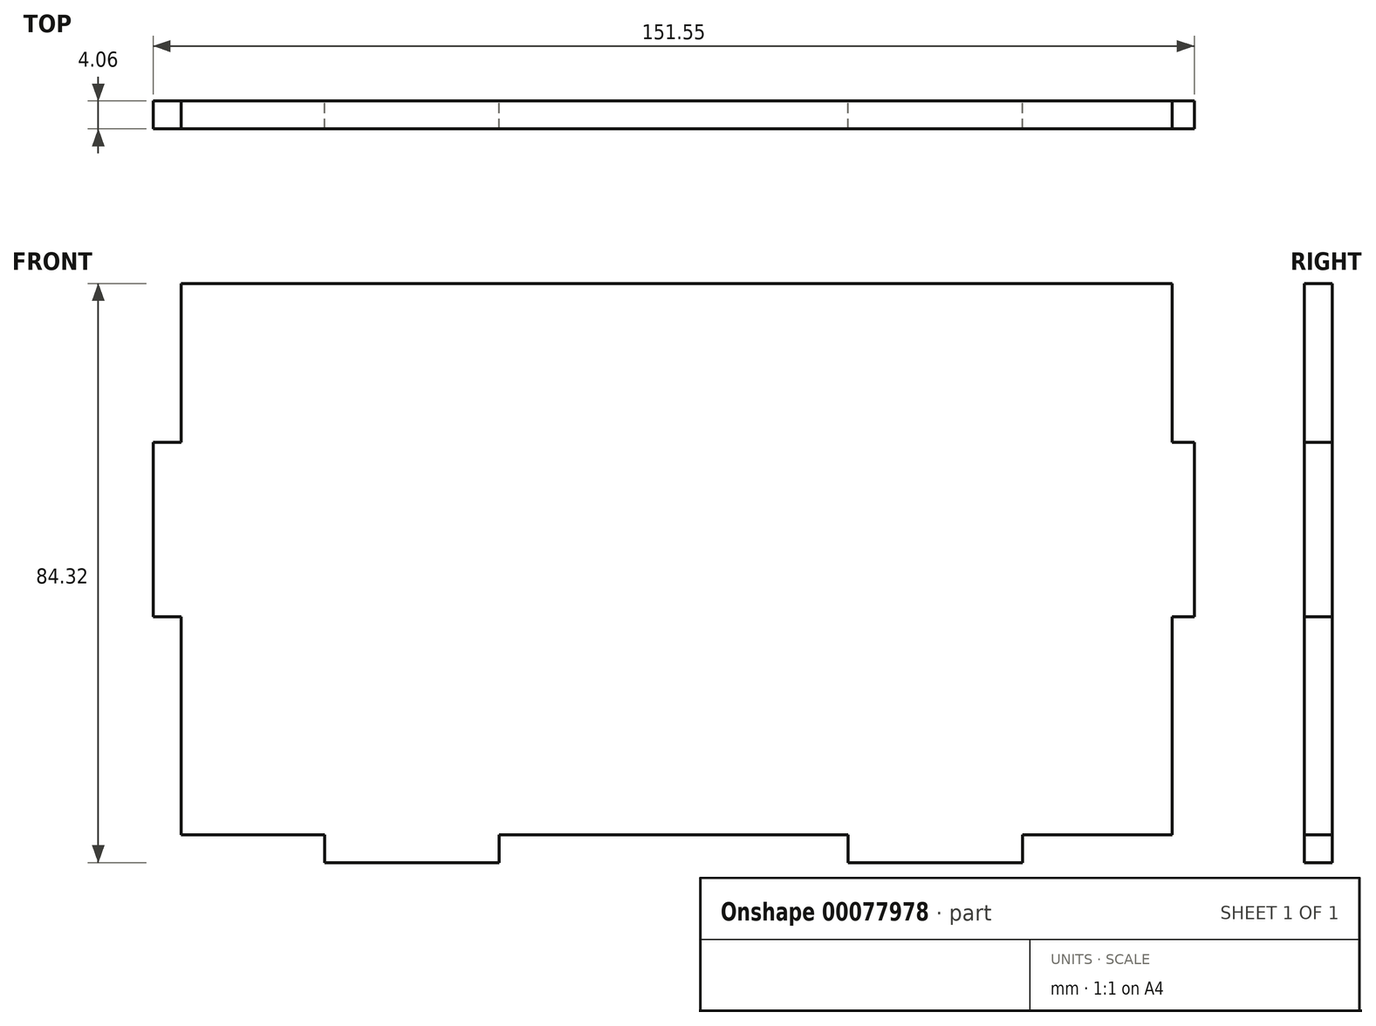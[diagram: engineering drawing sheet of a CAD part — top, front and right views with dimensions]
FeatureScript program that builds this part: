
annotation { "Feature Type Name" : "Feature", "Feature Type Description" : "" }
export const myFeature = defineFeature(function(context is Context, id is Id, definition is map)
    precondition{}
    {
        {
            var Q0;
            Q0=qCreatedBy(makeId("Front.planeOp"),FACE);
            var sketch = newSketch(context, id + "F0", { "sketchPlane" : qUnion([Q0])});
            skLineSegment(sketch, "E0.top", {"start": v(-104.23, 10.4) * mm, "end": v(-83.32, 10.4) * mm});
            skLineSegment(sketch, "E0.right", {"start": v(40.04, 86.6) * mm, "end": v(40.04, 67.55) * mm});
            skLineSegment(sketch, "E1.trimOffspring", {"start": v(-13.04, 10.4) * mm, "end": v(-7.12, 10.4) * mm});
            skPoint(sketch, "E2.orphan", {"position": v(-32.1, 10.4) * mm});
            skPoint(sketch, "E3.endSnap0", {"position": v(-32.1, 60.31) * mm});
            skLineSegment(sketch, "E4.top", {"start": v(-83.32, 90.66) * mm, "end": v(-57.92, 90.66) * mm});
            skLineSegment(sketch, "E5.top", {"start": v(-7.12, 90.66) * mm, "end": v(18.28, 90.66) * mm});
            skPoint(sketch, "E6.MirrorCS.end.orphan", {"position": v(18.28, 86.6) * mm});
            skLineSegment(sketch, "E7.MirrorCS", {"start": v(-83.32, 10.4) * mm, "end": v(-83.32, 6.34) * mm});
            skLineSegment(sketch, "E8.MirrorCS", {"start": v(-83.32, 6.34) * mm, "end": v(-57.92, 6.34) * mm});
            skLineSegment(sketch, "E9.MirrorCS", {"start": v(-57.92, 10.4) * mm, "end": v(-57.92, 6.34) * mm});
            skLineSegment(sketch, "E10.MirrorCS", {"start": v(-7.12, 10.4) * mm, "end": v(-7.12, 6.34) * mm});
            skLineSegment(sketch, "E11.MirrorCS", {"start": v(-7.12, 6.34) * mm, "end": v(18.28, 6.34) * mm});
            skLineSegment(sketch, "E12.MirrorCS", {"start": v(18.28, 10.4) * mm, "end": v(18.28, 6.34) * mm});
            skLineSegment(sketch, "E13.trimOffspring", {"start": v(-57.92, 10.4) * mm, "end": v(-51.57, 10.4) * mm});
            skLineSegment(sketch, "E14.trimOffspring", {"start": v(18.28, 10.4) * mm, "end": v(40.04, 10.4) * mm});
            skLineSegment(sketch, "E15.trimOffspring", {"start": v(-104.23, 34.02) * mm, "end": v(-104.23, 10.4) * mm});
            skLineSegment(sketch, "E16.trimOffspring", {"start": v(40.04, 34.02) * mm, "end": v(40.04, 10.4) * mm});
            skLineSegment(sketch, "E17", {"start": v(-104.23, 86.6) * mm, "end": v(-104.23, 67.55) * mm});
            skLineSegment(sketch, "E18", {"start": v(-104.23, 67.55) * mm, "end": v(-108.93, 67.55) * mm});
            skLineSegment(sketch, "E19", {"start": v(-108.3, 64.22) * mm, "end": v(-108.3, 67.55) * mm});
            skLineSegment(sketch, "E20.bottom", {"start": v(-108.3, 67.55) * mm, "end": v(-104.23, 67.55) * mm});
            skLineSegment(sketch, "E20.top", {"start": v(-108.3, 42.15) * mm, "end": v(-104.23, 42.15) * mm});
            skLineSegment(sketch, "E20.left", {"start": v(-108.3, 67.55) * mm, "end": v(-108.3, 42.15) * mm});
            skLineSegment(sketch, "E21.MirrorCS", {"start": v(43.26, 67.55) * mm, "end": v(39.2, 67.55) * mm});
            skLineSegment(sketch, "E22.MirrorCS", {"start": v(43.26, 67.55) * mm, "end": v(43.26, 42.15) * mm});
            skLineSegment(sketch, "E23.MirrorCS", {"start": v(40.04, 42.15) * mm, "end": v(43.26, 42.15) * mm});
            skLineSegment(sketch, "E24", {"start": v(40.04, 34.02) * mm, "end": v(40.04, 42.15) * mm});
            skLineSegment(sketch, "E25.trimOffspring", {"start": v(-104.23, 42.15) * mm, "end": v(-104.23, 34.02) * mm});
            skLineSegment(sketch, "E26.trimOffspring", {"start": v(-13.47, 10.4) * mm, "end": v(-13.04, 10.4) * mm});
            skLineSegment(sketch, "E27", {"start": v(-51.57, 10.4) * mm, "end": v(-13.04, 10.4) * mm});
            skLineSegment(sketch, "E28.top", {"start": v(-104.23, 90.66) * mm, "end": v(40.04, 90.66) * mm});
            skLineSegment(sketch, "E28.left", {"start": v(-104.23, 86.6) * mm, "end": v(-104.23, 90.66) * mm});
            skLineSegment(sketch, "E28.right", {"start": v(40.04, 86.6) * mm, "end": v(40.04, 90.66) * mm});
            skSolve(sketch);
        }
        {
            var Q0;
            Q0=makeQuery(id+"F0.imprint","IMPRINT",FACE,{"disambiguationData":[TD([[makeQuery(id+"F0.imprint","IMPRINT",EDGE,{"derivedFrom":sQuery(id+"F0.wireOp",EDGE,"E0.top")}),1.0]])]});
            var Q1;
            {var subQ2=sQuery(id+"F0.wireOp",EDGE,"E0.right");Q1=makeQuery(id+"F0.imprint","IMPRINT",FACE,{"disambiguationData":[TD([[makeQuery(id+"F0.imprint","IMPRINT",EDGE,{"derivedFrom":subQ2}),-1.0]])]});}
            extrude(context, id + "F1", {"entities" : qUnion([Q0, Q1]), "depth" : 4.06 * mm});
        }
    });
